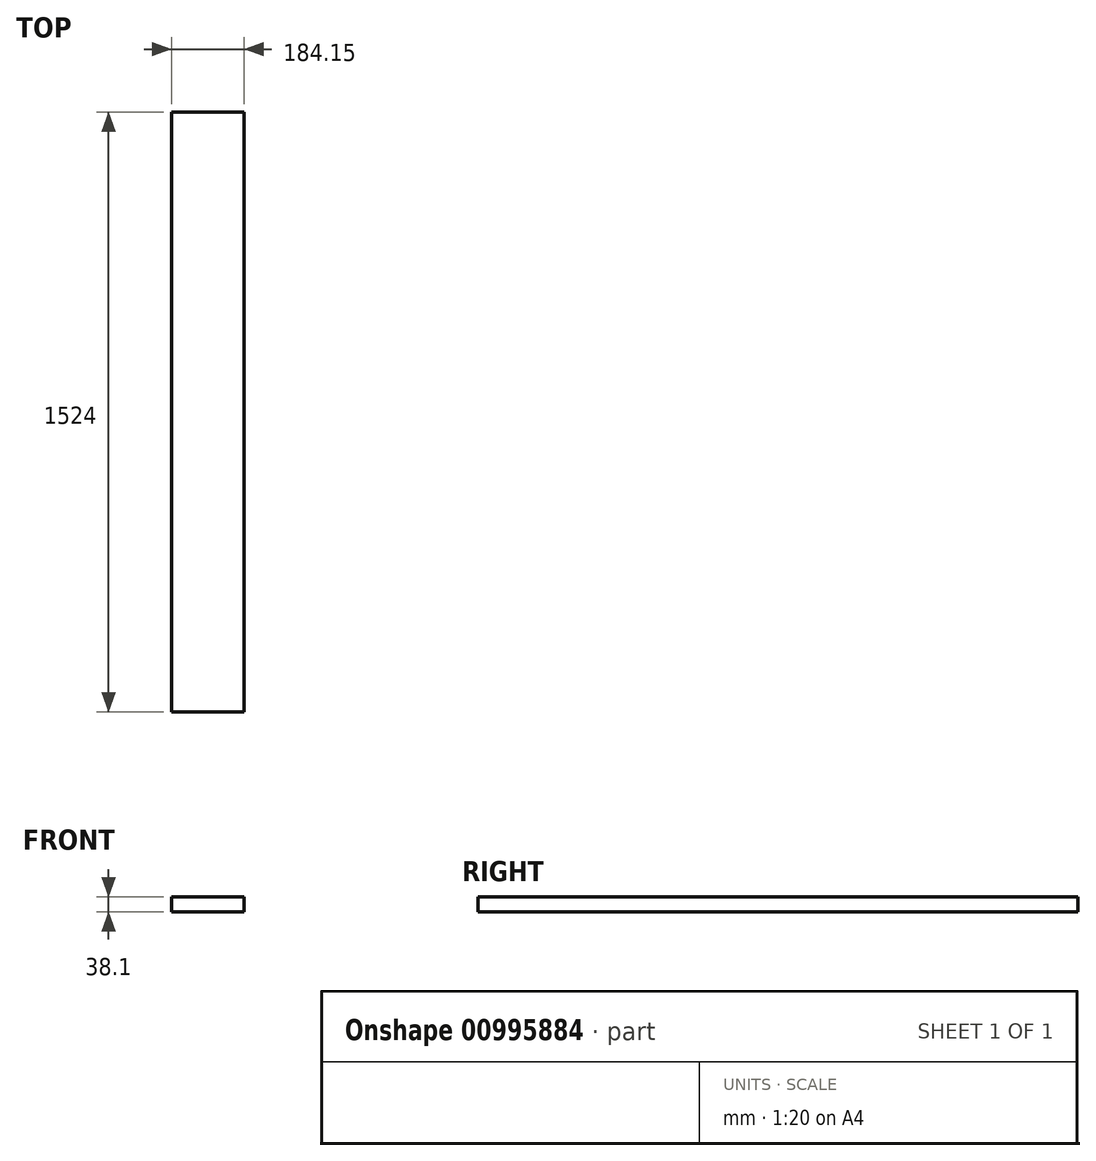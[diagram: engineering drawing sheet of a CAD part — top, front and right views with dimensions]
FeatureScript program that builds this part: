
annotation { "Feature Type Name" : "Feature", "Feature Type Description" : "" }
export const myFeature = defineFeature(function(context is Context, id is Id, definition is map)
    precondition{}
    {
        {
            var Q0;
            Q0=qCreatedBy(makeId("Front.planeOp"),FACE);
            var sketch = newSketch(context, id + "F0", { "sketchPlane" : qUnion([Q0])});
            skLineSegment(sketch, "E0.bottom", {"start": v(0, 0) * mm, "end": v(184.15, 0) * mm});
            skLineSegment(sketch, "E0.top", {"start": v(0, 38.1) * mm, "end": v(184.15, 38.1) * mm});
            skLineSegment(sketch, "E0.left", {"start": v(0, 0) * mm, "end": v(0, 38.1) * mm});
            skLineSegment(sketch, "E0.right", {"start": v(184.15, 0) * mm, "end": v(184.15, 38.1) * mm});
            skSolve(sketch);
        }
        {
            var Q0;
            Q0 = qSketchRegion(id + "F0", true);
            extrude(context, id + "F1", {"entities" : qUnion([Q0]), "depth" : 1524 * mm, "offsetDistance" : 25.4 * mm});
        }
    });
